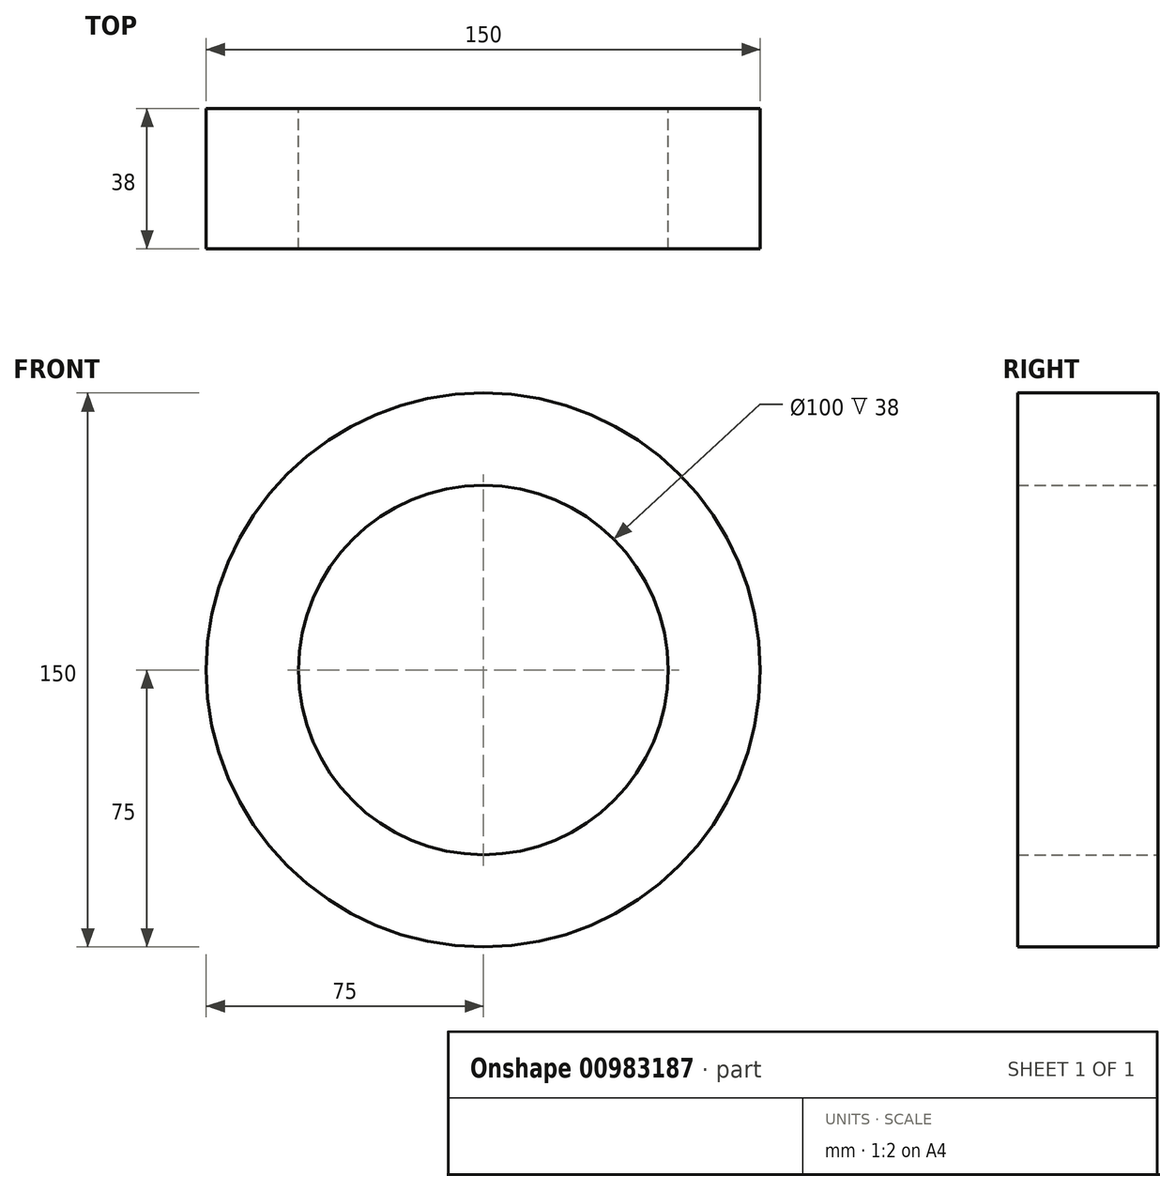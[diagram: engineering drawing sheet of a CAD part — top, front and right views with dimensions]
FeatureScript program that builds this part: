
annotation { "Feature Type Name" : "Feature", "Feature Type Description" : "" }
export const myFeature = defineFeature(function(context is Context, id is Id, definition is map)
    precondition{}
    {
        {
            var Q0;
            Q0=qCreatedBy(makeId("Front.planeOp"),FACE);
            var sketch = newSketch(context, id + "F0", { "sketchPlane" : qUnion([Q0])});
            skCircle(sketch, "E0", {"center": v(0, 0) * mm, "radius": 75 * mm});
            skCircle(sketch, "E1", {"center": v(0, 0) * mm, "radius": 50 * mm});
            skSolve(sketch);
        }
        {
            var Q0;
            Q0=makeQuery(id+"F0.imprint","IMPRINT",FACE,{"disambiguationData":[TD([[makeQuery(id+"F0.imprint","IMPRINT",EDGE,{"derivedFrom":sQuery(id+"F0.wireOp",EDGE,"E0")}),1.0]])]});
            extrude(context, id + "F1", {"entities" : qUnion([Q0]), "depth" : 38 * mm, "offsetDistance" : 25 * mm});
        }
    });
